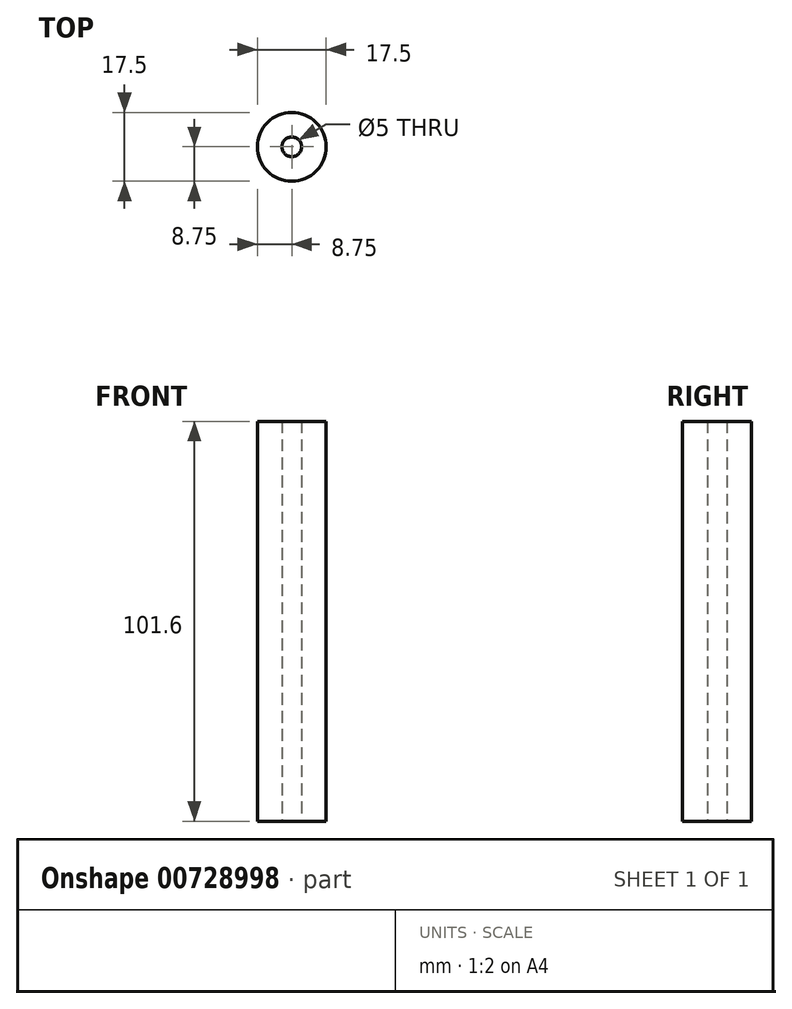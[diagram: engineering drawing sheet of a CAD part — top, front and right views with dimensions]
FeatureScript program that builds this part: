
annotation { "Feature Type Name" : "Feature", "Feature Type Description" : "" }
export const myFeature = defineFeature(function(context is Context, id is Id, definition is map)
    precondition{}
    {
        {
            var Q0;
            Q0=qCreatedBy(makeId("Top.planeOp"),FACE);
            var sketch = newSketch(context, id + "F0", { "sketchPlane" : qUnion([Q0])});
            skCircle(sketch, "E0", {"center": v(0, 0) * mm, "radius": 2.5 * mm});
            skCircle(sketch, "E1", {"center": v(0, 0) * mm, "radius": 8.75 * mm});
            skSolve(sketch);
        }
        {
            var Q0;
            Q0=makeQuery(id+"F0.imprint","IMPRINT",FACE,{"disambiguationData":[TD([[makeQuery(id+"F0.imprint","IMPRINT",EDGE,{"derivedFrom":sQuery(id+"F0.wireOp",EDGE,"E0")}),-1.0]])]});
            extrude(context, id + "F1", {"entities" : qUnion([Q0]), "depth" : 101.6 * mm, "offsetDistance" : 25.4 * mm});
        }
    });
